# Revit family: Mixer-Bath Shower-Dorf Enigma with Diverter-Round Trim1
name_source: partatom
category: Plumbing Fixtures
revit_build: Autodesk Revit 2015 (Build: 20160512_0715(x64)
units: mm (PartAtom-declared; Revit-internal decimal feet)

## types (2) — shared parameters
Assembly Code = D2020300
CW Connection = Yes
CWFU = 2
Connector Radius = 10 mm  [stored 0.0328084 ft]
Default Elevation = 1000 mm  [stored 3.28084 ft]
HW Connection = Yes
HWFU = 2
Height_ANZRS = 170 mm  [stored 0.557743 ft]
Length_ANZRS = 100 mm  [stored 0.328084 ft]
Manufacturer = GWA Bathrooms & Kitchens
ModifiedIssue_ANZRS = 20160616 $
Type Comments = Dorf Enigma Bath/Shower Mixer with Diverter Round Trim Kit
URL = http://specify.caroma.com.au
Vent Connection = No
Waste Connection = No
Width_ANZRS = 56 mm  [stored 0.183727 ft]
zero-valued in all types: Cost

## per-type parameters (varying)
| type | Material_ANZRS | Model |
| Chrome | Metal-Chrome-Caroma | 6490.04 |
| Black | Metal-Steel-Powdercoated-Matte Black | 6490.9 |

note: [stored X ft] marks values corroborated as IEEE doubles in the binary element streams (Revit-internal decimal feet)

## geometry (parser evidence)
native form markers: Blend x10, Sweep x2
no freeform markers — native parametric forms only
